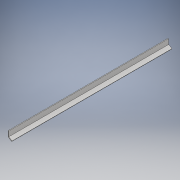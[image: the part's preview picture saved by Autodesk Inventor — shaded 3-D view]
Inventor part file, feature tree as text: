
AUTODESK INVENTOR PART (.ipt)
format: ipt  version: 2018 (Build 220112000, 112)  size: 99,840 bytes
history: native  units: mm
features: other x1, extrude x1, sketch x1
ambient origin geometry x8: Origin, YZ Plane, XZ Plane, XY Plane, X Axis, Y Axis, Z Axis, Center Point
bodies: Body1 (feature_tree)
feature tree (3):
  other  "ソリッド1"
  extrude  "押し出し1"  Depth=7.0mm
  sketch  "スケッチ1"
